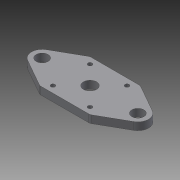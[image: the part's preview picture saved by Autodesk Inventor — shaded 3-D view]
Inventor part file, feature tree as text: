
AUTODESK INVENTOR PART (.ipt)
format: ipt  version: 2015 (Build 190159000, 159)  size: 124,416 bytes
history: native  units: in
note: dims shown in document units (in); Inventor stores cm internally (conversion verified against a paired STEP export)
features: extrude x2, sketch x2, fillet x1
ambient origin geometry x8: Origin, YZ Plane, XZ Plane, XY Plane, X Axis, Y Axis, Z Axis, Center Point
bodies: Body1 (feature_tree)
feature tree (5):
  extrude  "Extrusion4"  Depth=1.6535in
  extrude  "Extrusion5"  Depth=0.125in
  fillet  "Fillet1"  Radius=0.25in
  sketch  "Sketch1"  dims[d0=1.6535in d1=1.6535in]
  sketch  "Sketch2"  dims[d4=0.1378in d8=0.4331in d11=0.25in d12=0.0in d13=1.2205in d16=1.0in d17=0.0in d18=0.3937in d20=3.1496in d21=0.35in d22=0.125in]
